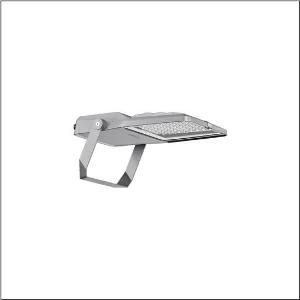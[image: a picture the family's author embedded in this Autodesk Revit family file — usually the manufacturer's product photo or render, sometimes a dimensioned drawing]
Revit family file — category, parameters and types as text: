
# Revit family: floodlight_fl_21_iq_mini___pl61_5xa7772b5c1a_2793
name_source: partatom
category: Lighting Fixtures
units: mm (PartAtom-declared; Revit-internal decimal feet)

## family parameters
Cut with Voids When Loaded = No
Host = Face
Light Source = No
Part Type = Normal
Room Calculation Point = No
Round Connector Dimension = Use Diameter
Shared = No

## types (1)
- --- (1 x LED, 5710 lm, 45.5 W, 4000K)
    Apparent Load = 46 VA
    CIE Flux Codes = 33 65 98 100 100
    Color Rendering = 80
    Color Temperature = 4000K
    Default Elevation = 1800 mm
    Description = Floodlight FL 21 iQ mini, floodlight, primary light control with lens, of PMMA, primary optical cover: protective disc, of toughened safety glass, transparent, light distribution: PL61, light emission: direct distribution, installation type: surface-mounted, LED, High Power LED, rated luminous flux: 5.710lm, luminous efficacy: 126lm/W, light colour: 840, colour temperature: 4000K, control: Street-Remote, Auto-Match, Temp-Guard, Night-Set, Smart-Wire, Desk-Remote (wireless, voltage-free reading and setting of iQ features in the workshop via application-optimized NFC function/RFID function), optimised constant luminous flux control (CLO 2.0), with terminal, 6-pole, mains connection: 220..240V, AC, 50/60Hz, start of lifetime: 46W, end of service life: 48W, reduction: 22W, luminaire housing, of diecast aluminium, powder-coated, Siteco® metallic grey (DB 702S), corrosivity category C5 mid according to DIN EN ISO 12944, sealing non-destructively replaceable, mounting bracket, of steel, galvanised, powder-coated, Siteco® metallic grey (DB 702S), protection rating (complete): IP66, insulation class (complete): insulation class II (safety insulation), certification: CE, ENEC, VDE, protection symbol: D, impact resistance: IK08, permissible operating ambient temperature: -40..+40°C, permissible operating ambient temperature for outdoor applications: -40..+50°C, standard: DIN EN 12944, LABS conformity tested according to VDMA 24364:2018-05, packaging unit: 1 piece

Light Distribution: PL61
    Height = 70 mm
    Lamp = 1 x LED
    Lamp Light Flux = 5710 lm
    Lamp Power = 45.5 W
    Lamp count = 1
    Length = 485 mm
    Luminous efficacy = 125 lm/W
    Manufacturer = Siteco
    ModVariant = No
    Model = 5XA7772B5C1A
    Number of Poles = 1
    OnlyDefault = Yes
    Power Factor = 1
    Product Name = Floodlight FL 21 iQ mini | PL61
    Product group = floodlight | pylon annexe
    ProductGroupID = 6200
    Protection Class = Protection class II
    Protection Degree = IP 66
    RLX_Detail_Level = 1
    RLX_Emergency_Light_Flux = 0 lm
    RLX_Emergency_Type = 0
    RLX_Emergency_Type_DB = No
    RlxData = <blob elided: 96193 chars, md5=30e7972d>
    Socket = socket
    Standby Power = 0 W
    System Light Flux = 5710 lm
    System Power = 46 W
    Type Comments = factory setting: luminous flux: 100 % | dim-lin: 254 | 463 mA
    Type Image = l_1006845.jpg
    URL = http://relux.com
    VarID = @adj_106479
    Voltage = 0 V
    Weight = 0.00 kg
    Width = 337 mm

## geometry (parser evidence)
native form markers: Blend x4, Sweep x10
no freeform markers — native parametric forms only
